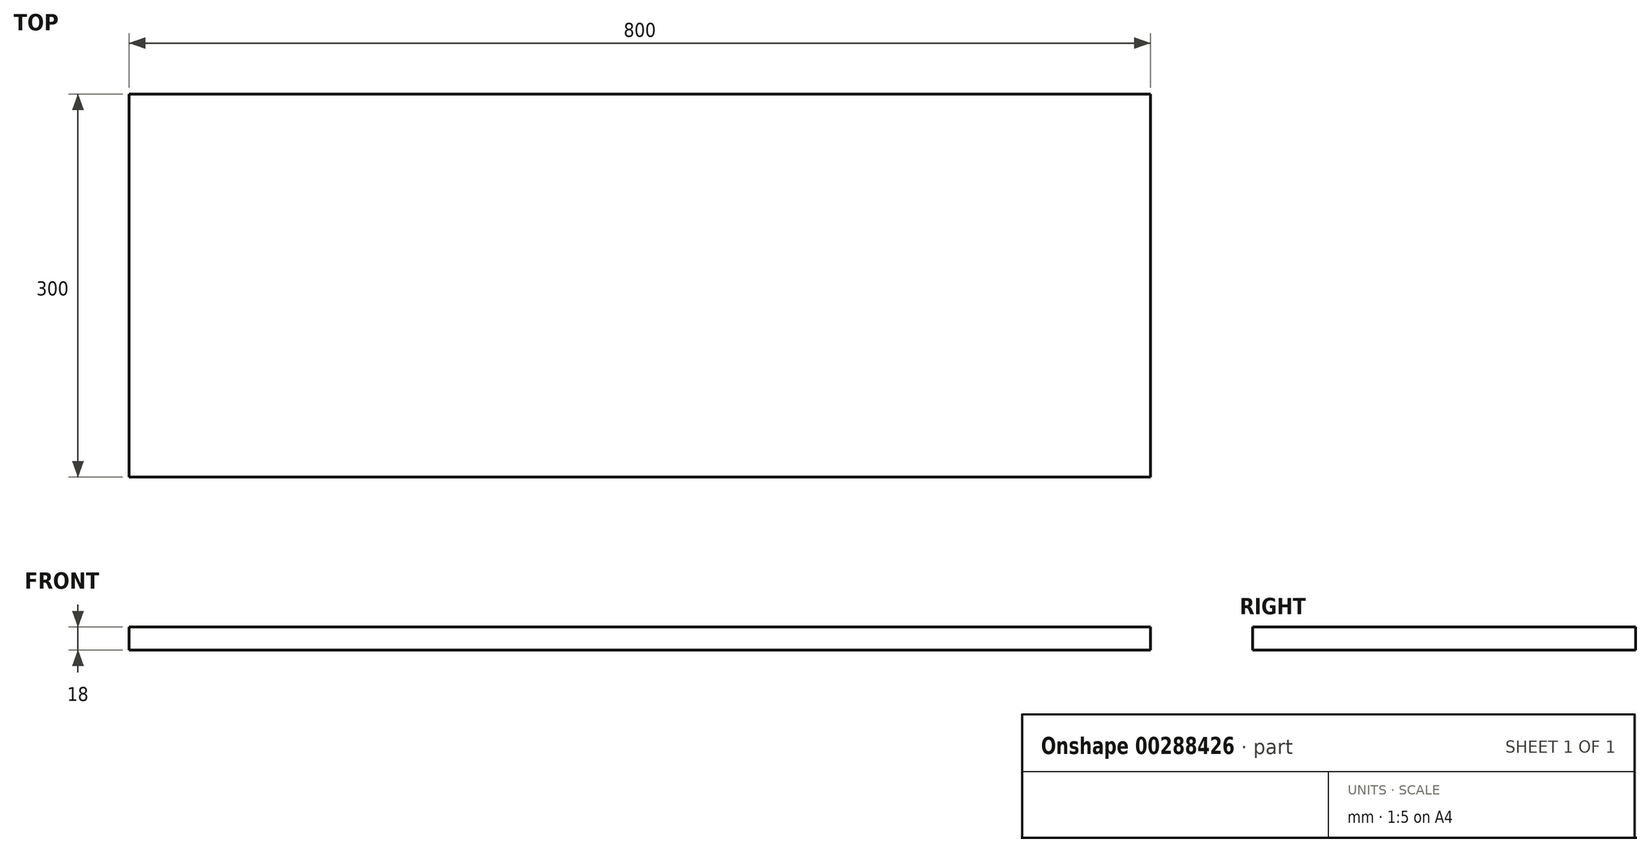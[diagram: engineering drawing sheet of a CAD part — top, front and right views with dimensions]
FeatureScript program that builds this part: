
annotation { "Feature Type Name" : "Feature", "Feature Type Description" : "" }
export const myFeature = defineFeature(function(context is Context, id is Id, definition is map)
    precondition{}
    {
        {
            var Q0;
            Q0=qCreatedBy(makeId("Front.planeOp"),FACE);
            var sketch = newSketch(context, id + "F0", { "sketchPlane" : qUnion([Q0])});
            skLineSegment(sketch, "E0.bottom", {"start": v(-111.47, -198.56) * mm, "end": v(688.53, -198.56) * mm});
            skLineSegment(sketch, "E0.top", {"start": v(-111.47, -180.56) * mm, "end": v(688.53, -180.56) * mm});
            skLineSegment(sketch, "E0.left", {"start": v(-111.47, -198.56) * mm, "end": v(-111.47, -180.56) * mm});
            skLineSegment(sketch, "E0.right", {"start": v(688.53, -198.56) * mm, "end": v(688.53, -180.56) * mm});
            skLineSegment(sketch, "E1", {"start": v(-378.21, 132.38) * mm, "end": v(-360.21, 132.38) * mm});
            skSolve(sketch);
        }
        {
            var Q0;
            Q0=makeQuery(id+"F0.imprint","IMPRINT",FACE,{"disambiguationData":[TD([[makeQuery(id+"F0.imprint","IMPRINT",EDGE,{"derivedFrom":sQuery(id+"F0.wireOp",EDGE,"E0.bottom")}),1.0]])]});
            extrude(context, id + "F1", {"entities" : qUnion([Q0]), "depth" : 300 * mm});
        }
    });
